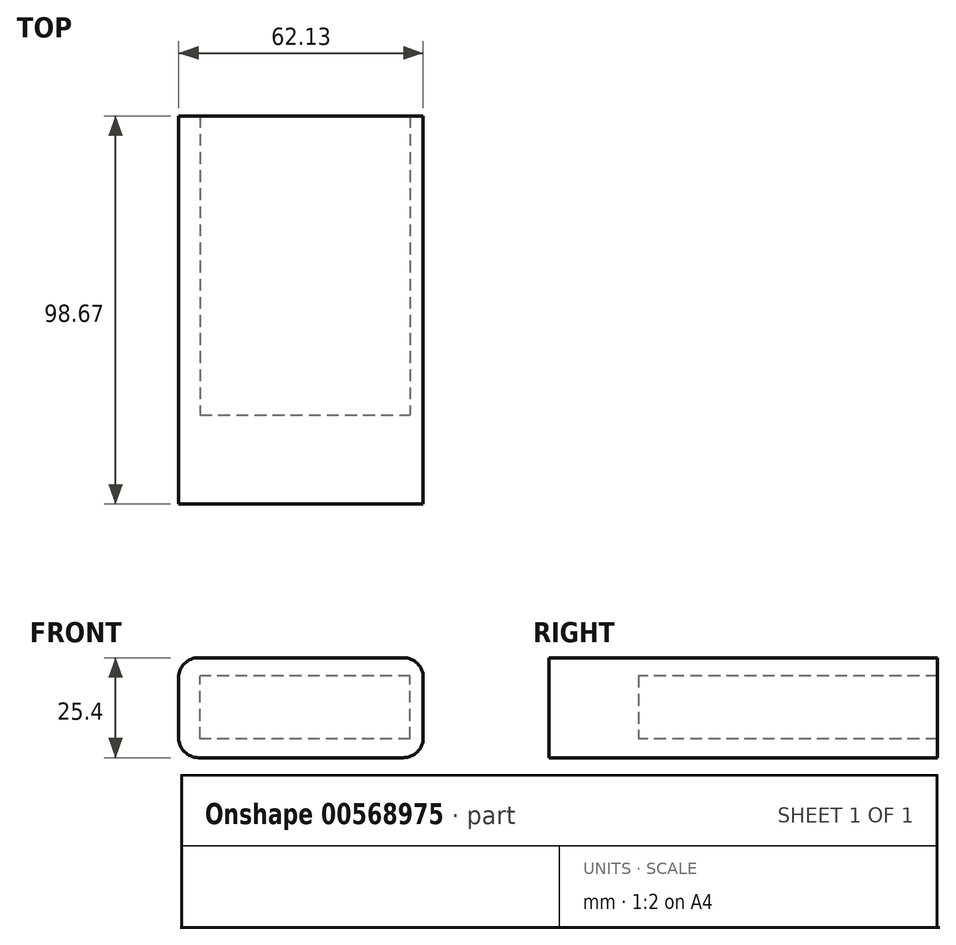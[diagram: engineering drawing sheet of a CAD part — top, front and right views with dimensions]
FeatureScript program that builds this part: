
annotation { "Feature Type Name" : "Feature", "Feature Type Description" : "" }
export const myFeature = defineFeature(function(context is Context, id is Id, definition is map)
    precondition{}
    {
        {
            var Q0;
            Q0=qCreatedBy(makeId("Top.planeOp"),FACE);
            var sketch = newSketch(context, id + "F0", { "sketchPlane" : qUnion([Q0])});
            skLineSegment(sketch, "E0.bottom", {"start": v(-29.5, 40.15) * mm, "end": v(32.63, 40.15) * mm});
            skLineSegment(sketch, "E0.top", {"start": v(-29.5, -58.52) * mm, "end": v(32.63, -58.52) * mm});
            skLineSegment(sketch, "E0.left", {"start": v(-29.5, 40.15) * mm, "end": v(-29.5, -58.52) * mm});
            skLineSegment(sketch, "E0.right", {"start": v(32.63, 40.15) * mm, "end": v(32.63, -58.52) * mm});
            skSolve(sketch);
        }
        {
            var Q0;
            Q0=makeQuery(id+"F0.imprint","IMPRINT",FACE,{"disambiguationData":[TD([[makeQuery(id+"F0.imprint","IMPRINT",EDGE,{"derivedFrom":sQuery(id+"F0.wireOp",EDGE,"E0.bottom")}),-1.0]])]});
            extrude(context, id + "F1", {"entities" : qUnion([Q0]), "depth" : 25.4 * mm, "offsetDistance" : 25.4 * mm});
        }
        {
            var Q0;
            Q0=qCreatedBy(makeId("Front.planeOp"),FACE);
            var sketch = newSketch(context, id + "F2", { "sketchPlane" : qUnion([Q0])});
            skLineSegment(sketch, "E1.bottom", {"start": v(-24.03, 20.8) * mm, "end": v(29.3, 20.8) * mm});
            skLineSegment(sketch, "E1.top", {"start": v(-24.03, 4.79) * mm, "end": v(29.3, 4.79) * mm});
            skLineSegment(sketch, "E1.left", {"start": v(-24.03, 20.8) * mm, "end": v(-24.03, 4.79) * mm});
            skLineSegment(sketch, "E1.right", {"start": v(29.3, 20.8) * mm, "end": v(29.3, 4.79) * mm});
            skSolve(sketch);
        }
        {
            var Q0;
            Q0 = qSketchRegion(id + "F2", true);
            extrude(context, id + "F3", {"entities" : qUnion([Q0]), "operationType" : NewBodyOperationType.REMOVE, "oppositeDirection" : true, "depth" : 159 * mm, "offsetDistance" : 25.4 * mm, "hasSecondDirection" : true, "secondDirectionOppositeDirection" : false, "secondDirectionDepth" : 35.81 * mm});
        }
        {
            var Q0;
            Q0=makeQuery(id+"F1.opExtrude","CAP_EDGE",EDGE,{"disambiguationData":[OSD([sQuery(id+"F0.wireOp",EDGE,"E0.right")])],"isStart":false});
            var Q1;
            Q1=makeQuery(id+"F1.opExtrude","CAP_EDGE",EDGE,{"disambiguationData":[OSD([sQuery(id+"F0.wireOp",EDGE,"E0.left")])],"isStart":false});
            var Q2;
            Q2=makeQuery(id+"F1.opExtrude","CAP_EDGE",EDGE,{"disambiguationData":[OSD([sQuery(id+"F0.wireOp",EDGE,"E0.left")])],"isStart":true});
            var Q3;
            Q3=makeQuery(id+"F1.opExtrude","CAP_EDGE",EDGE,{"disambiguationData":[OSD([sQuery(id+"F0.wireOp",EDGE,"E0.right")])],"isStart":true});
            fillet(context, id + "F4", {"entities" : qUnion([Q0, Q1, Q2, Q3]), "radius" : 5.08 * mm, "tangentPropagation" : true, "allowEdgeOverflow" : false});
        }
    });
